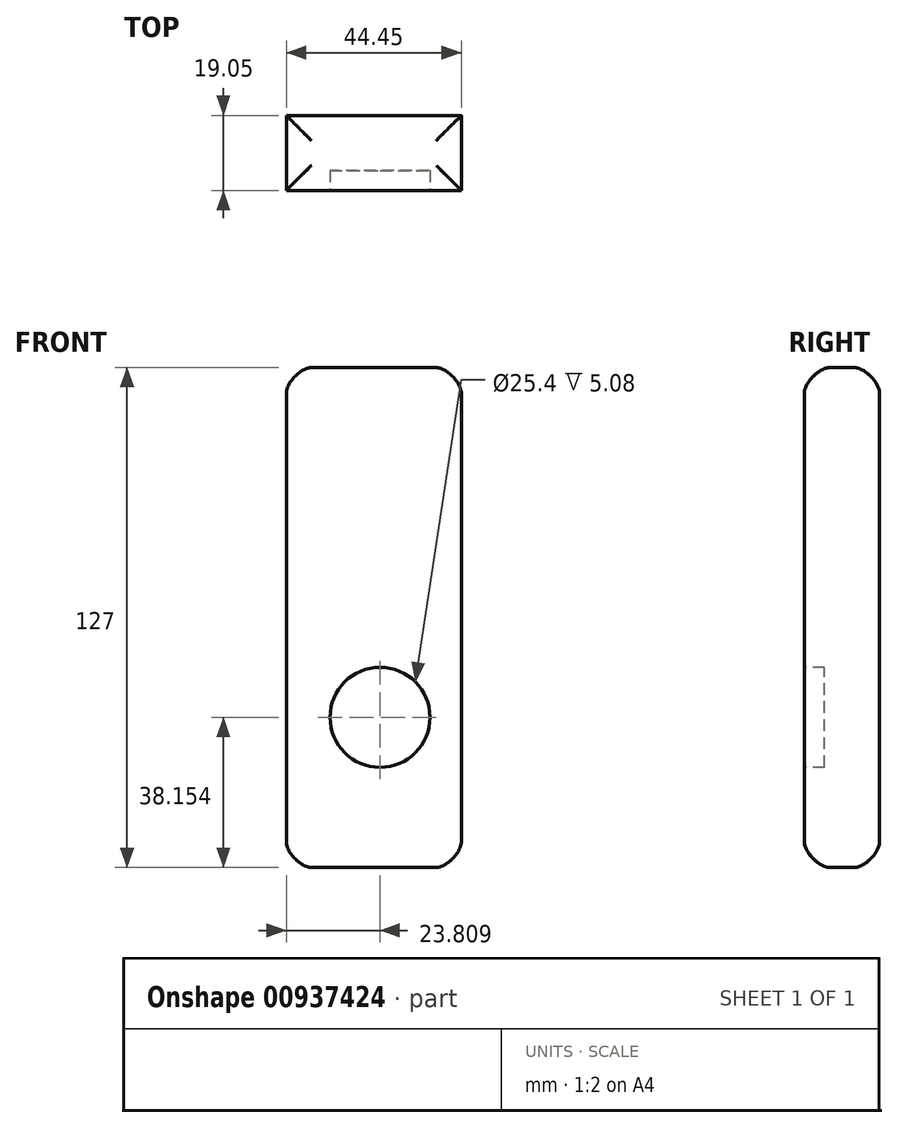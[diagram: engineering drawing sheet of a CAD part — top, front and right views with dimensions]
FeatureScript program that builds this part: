
annotation { "Feature Type Name" : "Feature", "Feature Type Description" : "" }
export const myFeature = defineFeature(function(context is Context, id is Id, definition is map)
    precondition{}
    {
        {
            var Q0;
            Q0=qCreatedBy(makeId("Front.planeOp"),FACE);
            var sketch = newSketch(context, id + "F0", { "sketchPlane" : qUnion([Q0])});
            skLineSegment(sketch, "E0.bottom", {"start": v(2.38, 0) * mm, "end": v(46.83, 0) * mm});
            skLineSegment(sketch, "E0.top", {"start": v(2.38, 127) * mm, "end": v(46.83, 127) * mm});
            skLineSegment(sketch, "E0.left", {"start": v(2.38, 0) * mm, "end": v(2.38, 127) * mm});
            skLineSegment(sketch, "E0.right", {"start": v(46.83, 0) * mm, "end": v(46.83, 127) * mm});
            skSolve(sketch);
        }
        {
            var Q0;
            Q0=makeQuery(id+"F0.imprint","IMPRINT",FACE,{"disambiguationData":[TD([[makeQuery(id+"F0.imprint","IMPRINT",EDGE,{"derivedFrom":sQuery(id+"F0.wireOp",EDGE,"E0.bottom")}),1.0]])]});
            extrude(context, id + "F1", {"entities" : qUnion([Q0]), "depth" : 19.05 * mm, "offsetDistance" : 25.4 * mm});
        }
        {
            var Q0;
            Q0=makeQuery(id+"F1.opExtrude","SWEPT_FACE",FACE,{"disambiguationData":[OSD([sQuery(id+"F0.wireOp",EDGE,"E0.top")])]});
            var Q1;
            Q1=makeQuery(id+"F1.opExtrude","SWEPT_FACE",FACE,{"disambiguationData":[OSD([sQuery(id+"F0.wireOp",EDGE,"E0.bottom")])]});
            fillet(context, id + "F2", {"entities" : qUnion([Q0, Q1]), "radius" : 6.35 * mm, "tangentPropagation" : true, "rho" : .3, "crossSection" : FilletCrossSection.CONIC, "allowEdgeOverflow" : false});
        }
        {
            var Q0;
            Q0=makeQuery(id+"F1.opExtrude","CAP_FACE",FACE,{"disambiguationData":[OSD([sQuery(id+"F0.wireOp",EDGE,"E0.bottom"),sQuery(id+"F0.wireOp",EDGE,"E0.top"),sQuery(id+"F0.wireOp",EDGE,"E0.left"),sQuery(id+"F0.wireOp",EDGE,"E0.right")])],"isStart":false});
            var sketch = newSketch(context, id + "F3", { "sketchPlane" : qUnion([Q0])});
            skCircle(sketch, "E1", {"center": v(26.19, 38.15) * mm, "radius": 12.7 * mm});
            skSolve(sketch);
        }
        {
            var Q0;
            Q0=makeQuery(id+"F3.imprint","IMPRINT",FACE,{"disambiguationData":[TD([[makeQuery(id+"F3.imprint","IMPRINT",EDGE,{"derivedFrom":sQuery(id+"F3.wireOp",EDGE,"E1")}),1.0]])]});
            extrude(context, id + "F4", {"entities" : qUnion([Q0]), "operationType" : NewBodyOperationType.REMOVE, "oppositeDirection" : true, "depth" : 5.08 * mm, "offsetDistance" : 25.4 * mm});
        }
    });
